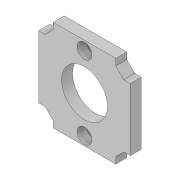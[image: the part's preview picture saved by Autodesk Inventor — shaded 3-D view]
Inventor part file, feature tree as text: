
AUTODESK INVENTOR PART (.ipt)
format: ipt  version: 2022 (Build 260153000, 153)  size: 201,216 bytes
history: native  units: mm
features: extrude x3, sketch x3, projected_geometry x2
ambient origin geometry x8: Origin, YZ Plane, XZ Plane, XY Plane, X Axis, Y Axis, Z Axis, Center Point
bodies: Solid1 (feature_tree)
feature tree (8):
  extrude  "Extrusion1"  Depth=24.9mm
  extrude  "IM_offset"  Depth=26.9mm
  extrude  "Extrusion4"  Depth=6.0mm TaperAngle=0.0deg
  sketch  "Sketch1"  dims[d0=45.0deg d2=24.9mm]
  sketch  "Sketch4"  dims[d3=3.14mm d4=26.9mm]
  projected_geometry  "Projected Loop4"
  sketch  "Skizze5"  dims[d5=25.0mm d6=6.0mm d7=0.0mm d19=0.2mm d20=10.0mm d21=0.0mm d22=40.0mm d23=8.1mm d24=8.1mm d25=5.0mm d26=-0.174533mm]
  projected_geometry  "Projizierte Kontur5"
